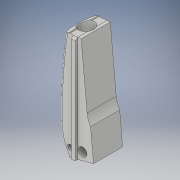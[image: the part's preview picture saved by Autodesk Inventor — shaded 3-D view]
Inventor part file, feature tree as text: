
AUTODESK INVENTOR PART (.ipt)
format: ipt  version: 2018.3 (Build 223284000, 284)  size: 233,984 bytes
history: native  units: in
note: dims shown in document units (in); Inventor stores cm internally (conversion verified against a paired STEP export)
features: extrude x4, chamfer x3, sketch x2, plane x1, fillet x1
ambient origin geometry x8: Origin, YZ Plane, XZ Plane, XY Plane, X Axis, Y Axis, Z Axis, Center Point
bodies: Solid1 (feature_tree)
feature tree (11):
  sketch  "Sketch1"  dims[d20=0.0378in d21=0.21in]
  extrude  "Extrusion1"  Depth=0.21in
  plane  "Work Plane2"
  sketch  "Sketch3"  dims[d22=90.0deg d23=1.9in d24=1.792in d25=1.14in d26=0.844in d27=0.19in d28=0.16in d29=0.6803in d30=0.376in d32=0.0378in d33=0.09in d35=22.5deg d37=1.765in d38=18.0in d39=0.9345in d40=1.94in d41=0.265in d42=0.044in d43=0.538in d44=0.0in d54=0.078in d55=0.0in d56=0.622in d57=0.622in d58=0.0in d59=0.0in d60=0.28in d61=0.174in d62=0.311in d63=1.672in d64=0.0in d65=0.0in d66=0.094in d67=0.233in d68=0.155in d69=0.7485in d70=0.0in d73=0.125in d74=0.125in d75=0.1718in d76=0.125in d77=0.125in d78=0.1718in d79=0.05in d80=0.04in d81=0.125in d82=0.1718in]
  extrude  "Extrusion3"  Depth=0.05in
  extrude  "Extrusion4"  Depth=0.05in
  extrude  "Extrusion5"  Depth=0.05in
  chamfer  "Chamfer1"  Distance=0.844in
  chamfer  "Chamfer2"  Distance=0.19in
  fillet  "Fillet2"  Radius=0.16in
  chamfer  "Chamfer3"  Distance=0.6803in
